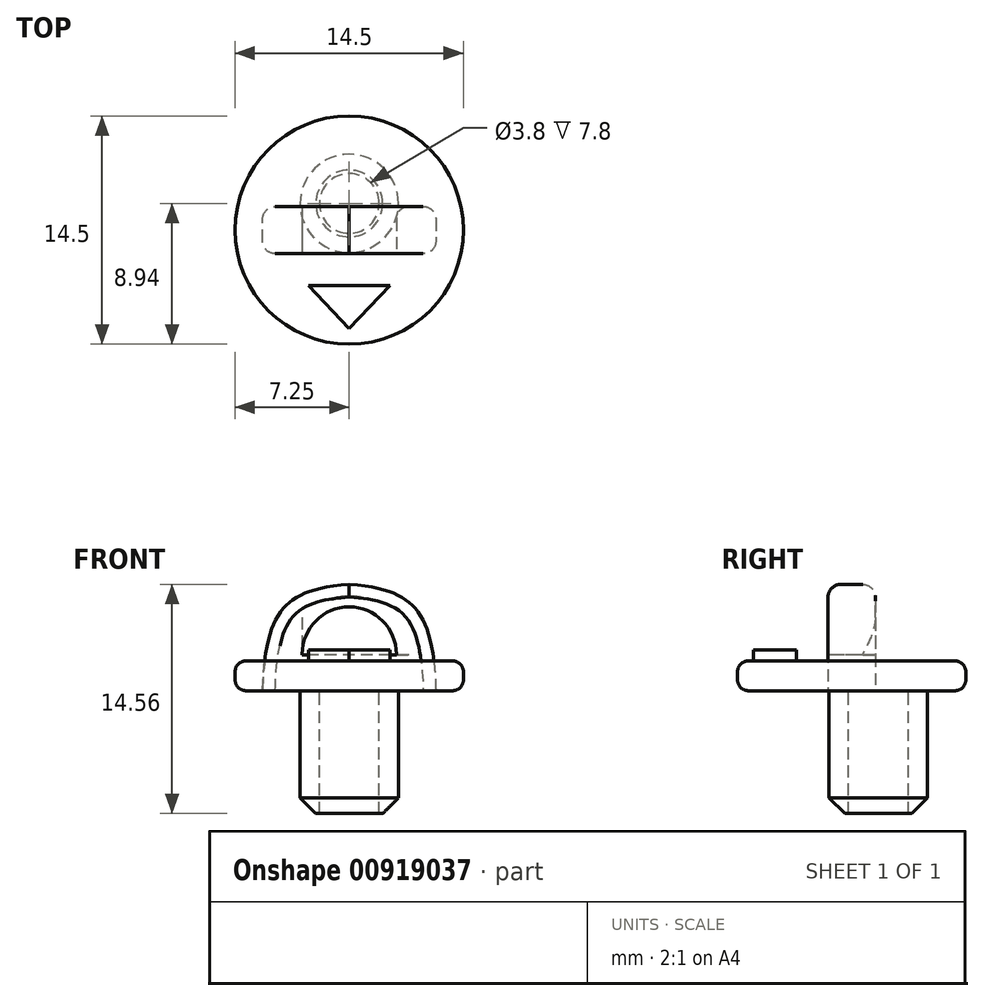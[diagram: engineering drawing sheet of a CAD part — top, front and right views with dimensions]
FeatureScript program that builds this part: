
annotation { "Feature Type Name" : "Feature", "Feature Type Description" : "" }
export const myFeature = defineFeature(function(context is Context, id is Id, definition is map)
    precondition{}
    {
        {
            var Q0;
            Q0=qCreatedBy(makeId("Top.planeOp"),FACE);
            var sketch = newSketch(context, id + "F0", { "sketchPlane" : qUnion([Q0])});
            skCircle(sketch, "E0", {"center": v(0, 0) * mm, "radius": 1.9 * mm});
            skCircle(sketch, "E1", {"center": v(0, 0) * mm, "radius": 3.12 * mm});
            skCircle(sketch, "E2", {"center": v(0, -1.7) * mm, "radius": 7.25 * mm});
            skLineSegment(sketch, "E3.bottom", {"start": v(-5.5, -3.2) * mm, "end": v(5.5, -3.2) * mm});
            skLineSegment(sketch, "E3.top", {"start": v(-5.5, -0.2) * mm, "end": v(5.5, -0.2) * mm});
            skLineSegment(sketch, "E3.left", {"start": v(-5.5, -3.2) * mm, "end": v(-5.5, -0.2) * mm});
            skLineSegment(sketch, "E3.right", {"start": v(5.5, -3.2) * mm, "end": v(5.5, -0.2) * mm});
            skLineSegment(sketch, "E4", {"start": v(0, -7.94) * mm, "end": v(-2.58, -5.2) * mm});
            skLineSegment(sketch, "E5", {"start": v(-2.58, -5.2) * mm, "end": v(2.58, -5.2) * mm});
            skLineSegment(sketch, "E6", {"start": v(2.58, -5.2) * mm, "end": v(0, -7.94) * mm});
            skSolve(sketch);
        }
        {
            var Q0;
            {var subQ0=sQuery(id+"F0.wireOp",EDGE,"E3.bottom");var subQ1=sQuery(id+"F0.wireOp",EDGE,"E0");var subQ2=makeQuery(id+"F0.imprint","INTERSECT",VERTEX,{"disambiguationData":[OD(0.0)],"derivedFrom":[subQ1,subQ0]});Q0=makeQuery(id+"F0.imprint","IMPRINT",FACE,{"disambiguationData":[TD([[makeQuery(id+"F0.imprint","IMPRINT",EDGE,{"disambiguationData":[TD([[subQ2,-1.0]])],"derivedFrom":subQ1}),-1.0]])]});}
            var Q1;
            {var subQ0=sQuery(id+"F0.wireOp",EDGE,"E3.top");var subQ1=sQuery(id+"F0.wireOp",EDGE,"E0");var subQ2=makeQuery(id+"F0.imprint","INTERSECT",VERTEX,{"disambiguationData":[OD(1.0)],"derivedFrom":[subQ1,subQ0]});Q1=makeQuery(id+"F0.imprint","IMPRINT",FACE,{"disambiguationData":[TD([[makeQuery(id+"F0.imprint","IMPRINT",EDGE,{"disambiguationData":[TD([[subQ2,1.0]])],"derivedFrom":subQ1}),-1.0]])]});}
            var Q2;
            {var subQ0=sQuery(id+"F0.wireOp",EDGE,"E3.top");var subQ1=sQuery(id+"F0.wireOp",EDGE,"E0");var subQ2=makeQuery(id+"F0.imprint","INTERSECT",VERTEX,{"disambiguationData":[OD(0.0)],"derivedFrom":[subQ1,subQ0]});Q2=makeQuery(id+"F0.imprint","IMPRINT",FACE,{"disambiguationData":[TD([[makeQuery(id+"F0.imprint","IMPRINT",EDGE,{"disambiguationData":[TD([[subQ2,1.0]])],"derivedFrom":subQ1}),-1.0]])]});}
            var Q3;
            {var subQ0=sQuery(id+"F0.wireOp",EDGE,"E3.top");var subQ1=sQuery(id+"F0.wireOp",EDGE,"E0");var subQ2=makeQuery(id+"F0.imprint","INTERSECT",VERTEX,{"disambiguationData":[OD(0.0)],"derivedFrom":[subQ1,subQ0]});Q3=makeQuery(id+"F0.imprint","IMPRINT",FACE,{"disambiguationData":[TD([[makeQuery(id+"F0.imprint","IMPRINT",EDGE,{"disambiguationData":[TD([[subQ2,-1.0]])],"derivedFrom":subQ1}),-1.0]])]});}
            extrude(context, id + "F1", {"entities" : qUnion([Q0, Q1, Q2, Q3]), "oppositeDirection" : true, "depth" : 7.8 * mm, "offsetDistance" : 25 * mm});
        }
        {
            var Q0;
            {var subQ0=sQuery(id+"F0.wireOp",EDGE,"E3.top");var subQ1=sQuery(id+"F0.wireOp",EDGE,"E0");var subQ2=makeQuery(id+"F0.imprint","INTERSECT",VERTEX,{"disambiguationData":[OD(0.0)],"derivedFrom":[subQ1,subQ0]});Q0=makeQuery(id+"F0.imprint","IMPRINT",FACE,{"disambiguationData":[TD([[makeQuery(id+"F0.imprint","IMPRINT",EDGE,{"disambiguationData":[TD([[subQ2,1.0]])],"derivedFrom":subQ1}),-1.0]])]});}
            var Q1;
            Q1=makeQuery(id+"F0.imprint","IMPRINT",FACE,{"disambiguationData":[TD([[makeQuery(id+"F0.imprint","IMPRINT",EDGE,{"derivedFrom":sQuery(id+"F0.wireOp",EDGE,"E2")}),1.0]])]});
            var Q2;
            {var subQ5=sQuery(id+"F0.wireOp",EDGE,"E3.left");Q2=makeQuery(id+"F0.imprint","IMPRINT",FACE,{"disambiguationData":[TD([[makeQuery(id+"F0.imprint","IMPRINT",EDGE,{"derivedFrom":subQ5}),-1.0]])]});}
            var Q3;
            {var subQ5=sQuery(id+"F0.wireOp",EDGE,"E3.right");Q3=makeQuery(id+"F0.imprint","IMPRINT",FACE,{"disambiguationData":[TD([[makeQuery(id+"F0.imprint","IMPRINT",EDGE,{"derivedFrom":subQ5}),1.0]])]});}
            var Q4;
            {var subQ0=sQuery(id+"F0.wireOp",EDGE,"E3.bottom");var subQ1=sQuery(id+"F0.wireOp",EDGE,"E0");var subQ2=makeQuery(id+"F0.imprint","INTERSECT",VERTEX,{"disambiguationData":[OD(0.0)],"derivedFrom":[subQ1,subQ0]});Q4=makeQuery(id+"F0.imprint","IMPRINT",FACE,{"disambiguationData":[TD([[makeQuery(id+"F0.imprint","IMPRINT",EDGE,{"disambiguationData":[TD([[subQ2,-1.0]])],"derivedFrom":subQ1}),-1.0]])]});}
            var Q5;
            {var subQ0=sQuery(id+"F0.wireOp",EDGE,"E3.top");var subQ1=sQuery(id+"F0.wireOp",EDGE,"E0");var subQ2=makeQuery(id+"F0.imprint","INTERSECT",VERTEX,{"disambiguationData":[OD(1.0)],"derivedFrom":[subQ1,subQ0]});Q5=makeQuery(id+"F0.imprint","IMPRINT",FACE,{"disambiguationData":[TD([[makeQuery(id+"F0.imprint","IMPRINT",EDGE,{"disambiguationData":[TD([[subQ2,1.0]])],"derivedFrom":subQ1}),-1.0]])]});}
            var Q6;
            {var subQ0=sQuery(id+"F0.wireOp",EDGE,"E3.top");var subQ1=sQuery(id+"F0.wireOp",EDGE,"E0");var subQ2=makeQuery(id+"F0.imprint","INTERSECT",VERTEX,{"disambiguationData":[OD(0.0)],"derivedFrom":[subQ1,subQ0]});Q6=makeQuery(id+"F0.imprint","IMPRINT",FACE,{"disambiguationData":[TD([[makeQuery(id+"F0.imprint","IMPRINT",EDGE,{"disambiguationData":[TD([[subQ2,-1.0]])],"derivedFrom":subQ1}),-1.0]])]});}
            var Q7;
            {var subQ0=sQuery(id+"F0.wireOp",EDGE,"E3.top");var subQ1=sQuery(id+"F0.wireOp",EDGE,"E0");var subQ2=makeQuery(id+"F0.imprint","INTERSECT",VERTEX,{"disambiguationData":[OD(0.0)],"derivedFrom":[subQ1,subQ0]});Q7=makeQuery(id+"F0.imprint","IMPRINT",FACE,{"disambiguationData":[TD([[makeQuery(id+"F0.imprint","IMPRINT",EDGE,{"disambiguationData":[TD([[subQ2,-1.0]])],"derivedFrom":subQ1}),1.0]])]});}
            var Q8;
            {var subQ0=sQuery(id+"F0.wireOp",EDGE,"E3.bottom");var subQ1=sQuery(id+"F0.wireOp",EDGE,"E0");var subQ2=makeQuery(id+"F0.imprint","INTERSECT",VERTEX,{"disambiguationData":[OD(0.0)],"derivedFrom":[subQ1,subQ0]});Q8=makeQuery(id+"F0.imprint","IMPRINT",FACE,{"disambiguationData":[TD([[makeQuery(id+"F0.imprint","IMPRINT",EDGE,{"disambiguationData":[TD([[subQ2,-1.0]])],"derivedFrom":subQ1}),1.0]])]});}
            var Q9;
            {var subQ0=sQuery(id+"F0.wireOp",EDGE,"E3.top");var subQ1=sQuery(id+"F0.wireOp",EDGE,"E0");var subQ2=makeQuery(id+"F0.imprint","INTERSECT",VERTEX,{"disambiguationData":[OD(0.0)],"derivedFrom":[subQ1,subQ0]});Q9=makeQuery(id+"F0.imprint","IMPRINT",FACE,{"disambiguationData":[TD([[makeQuery(id+"F0.imprint","IMPRINT",EDGE,{"disambiguationData":[TD([[subQ2,1.0]])],"derivedFrom":subQ1}),1.0]])]});}
            var Q10;
            Q10=makeQuery(id+"F0.imprint","IMPRINT",FACE,{"disambiguationData":[TD([[makeQuery(id+"F0.imprint","IMPRINT",EDGE,{"derivedFrom":sQuery(id+"F0.wireOp",EDGE,"E4")}),-1.0]])]});
            extrude(context, id + "F2", {"entities" : qUnion([Q0, Q1, Q2, Q3, Q4, Q5, Q6, Q7, Q8, Q9, Q10]), "depth" : 1.9 * mm, "offsetDistance" : 25 * mm});
        }
        {
            var Q0;
            {var subQ5=sQuery(id+"F0.wireOp",EDGE,"E3.right");Q0=makeQuery(id+"F0.imprint","IMPRINT",FACE,{"disambiguationData":[TD([[makeQuery(id+"F0.imprint","IMPRINT",EDGE,{"derivedFrom":subQ5}),1.0]])]});}
            var Q1;
            {var subQ5=sQuery(id+"F0.wireOp",EDGE,"E3.left");Q1=makeQuery(id+"F0.imprint","IMPRINT",FACE,{"disambiguationData":[TD([[makeQuery(id+"F0.imprint","IMPRINT",EDGE,{"derivedFrom":subQ5}),-1.0]])]});}
            var Q2;
            {var subQ0=sQuery(id+"F0.wireOp",EDGE,"E3.top");var subQ1=sQuery(id+"F0.wireOp",EDGE,"E0");var subQ2=makeQuery(id+"F0.imprint","INTERSECT",VERTEX,{"disambiguationData":[OD(0.0)],"derivedFrom":[subQ1,subQ0]});Q2=makeQuery(id+"F0.imprint","IMPRINT",FACE,{"disambiguationData":[TD([[makeQuery(id+"F0.imprint","IMPRINT",EDGE,{"disambiguationData":[TD([[subQ2,-1.0]])],"derivedFrom":subQ1}),-1.0]])]});}
            var Q3;
            {var subQ0=sQuery(id+"F0.wireOp",EDGE,"E3.top");var subQ1=sQuery(id+"F0.wireOp",EDGE,"E0");var subQ2=makeQuery(id+"F0.imprint","INTERSECT",VERTEX,{"disambiguationData":[OD(0.0)],"derivedFrom":[subQ1,subQ0]});Q3=makeQuery(id+"F0.imprint","IMPRINT",FACE,{"disambiguationData":[TD([[makeQuery(id+"F0.imprint","IMPRINT",EDGE,{"disambiguationData":[TD([[subQ2,-1.0]])],"derivedFrom":subQ1}),1.0]])]});}
            var Q4;
            {var subQ0=sQuery(id+"F0.wireOp",EDGE,"E3.top");var subQ1=sQuery(id+"F0.wireOp",EDGE,"E0");var subQ2=makeQuery(id+"F0.imprint","INTERSECT",VERTEX,{"disambiguationData":[OD(1.0)],"derivedFrom":[subQ1,subQ0]});Q4=makeQuery(id+"F0.imprint","IMPRINT",FACE,{"disambiguationData":[TD([[makeQuery(id+"F0.imprint","IMPRINT",EDGE,{"disambiguationData":[TD([[subQ2,1.0]])],"derivedFrom":subQ1}),-1.0]])]});}
            extrude(context, id + "F3", {"entities" : qUnion([Q0, Q1, Q2, Q3, Q4]), "depth" : 6.8 * mm, "offsetDistance" : 25 * mm});
        }
        {
            var Q0;
            Q0=makeQuery(id+"F3.opExtrude","CAP_EDGE",EDGE,{"disambiguationData":[OSD([sQuery(id+"F0.wireOp",EDGE,"E3.left")])],"isStart":false});
            var Q1;
            Q1=makeQuery(id+"F3.opExtrude","CAP_EDGE",EDGE,{"disambiguationData":[OSD([sQuery(id+"F0.wireOp",EDGE,"E3.right")])],"isStart":false});
            fillet(context, id + "F4", {"entities" : qUnion([Q0, Q1]), "radius" : 7 * mm, "tangentPropagation" : true, "rho" : .6, "crossSection" : FilletCrossSection.CONIC, "allowEdgeOverflow" : false});
        }
        {
            var Q0;
            Q0=makeQuery(id+"F3.opExtrude","SWEPT_FACE",FACE,{"disambiguationData":[OSD([sQuery(id+"F0.wireOp",EDGE,"E3.bottom")])]});
            var sketch = newSketch(context, id + "F5", { "sketchPlane" : qUnion([Q0])});
            skLineSegment(sketch, "E7.bottom", {"start": v(-3, 2.29) * mm, "end": v(3, 2.29) * mm});
            skLineSegment(sketch, "E7.top", {"start": v(0, 5.33) * mm, "end": v(0, 5.33) * mm});
            skLineSegment(sketch, "E7.left", {"start": v(-3, 2.29) * mm, "end": v(-3, 2.33) * mm});
            skLineSegment(sketch, "E7.right", {"start": v(3, 2.29) * mm, "end": v(3, 2.33) * mm});
            skPoint(sketch, "E7.middle", {"position": v(0, 3.8) * mm});
            skPoint(sketch, "E8.visualSharp", {"position": v(-3, 5.33) * mm});
            skArc(sketch, "E8.filletArc", {"start": v(0, 5.33) * mm, "mid": v(-2.11, 4.45) * mm, "end": v(-3, 2.33) * mm});
            skPoint(sketch, "E9.visualSharp", {"position": v(3, 5.33) * mm});
            skArc(sketch, "E9.filletArc", {"start": v(3, 2.33) * mm, "mid": v(2.11, 4.45) * mm, "end": v(0, 5.33) * mm});
            skSolve(sketch);
        }
        {
            var Q0;
            Q0=makeQuery(id+"F5.imprint","IMPRINT",FACE,{"disambiguationData":[TD([[makeQuery(id+"F5.imprint","IMPRINT",EDGE,{"derivedFrom":sQuery(id+"F5.wireOp",EDGE,"E7.bottom")}),1.0]])]});
            extrude(context, id + "F6", {"entities" : qUnion([Q0]), "operationType" : NewBodyOperationType.REMOVE, "oppositeDirection" : true, "depth" : 25 * mm, "offsetDistance" : 25 * mm});
        }
        {
            var Q0;
            Q0=makeQuery(id+"F6.boolean.opBoolean","COPY",EDGE,{"derivedFrom":makeQuery(id+"F6.opExtrude","CAP_EDGE",EDGE,{"disambiguationData":[OSD([sQuery(id+"F5.wireOp",EDGE,"E7.bottom")])],"isStart":true})});
            var Q1;
            Q1=makeQuery(id+"F6.boolean.opBoolean","COPY",EDGE,{"derivedFrom":makeQuery(id+"F6.opExtrude","CAP_EDGE",EDGE,{"disambiguationData":[OSD([sQuery(id+"F5.wireOp",EDGE,"E7.top")])],"isStart":true})});
            var Q2;
            Q2=makeQuery(id+"F6.boolean.opBoolean","COPY",EDGE,{"derivedFrom":makeQuery(id+"F6.opExtrude","CAP_EDGE",EDGE,{"disambiguationData":[OSD([sQuery(id+"F5.wireOp",EDGE,"E8.filletArc")])],"isStart":true})});
            var Q3;
            Q3=makeQuery(id+"F6.boolean.opBoolean","INTERSECT",EDGE,{"derivedFrom":[makeQuery(id+"F3.opExtrude","SWEPT_FACE",FACE,{"disambiguationData":[OSD([sQuery(id+"F0.wireOp",EDGE,"E3.top")])]}),makeQuery(id+"F6.opExtrude","SWEPT_FACE",FACE,{"disambiguationData":[OSD([sQuery(id+"F5.wireOp",EDGE,"E9.filletArc")])]})]});
            var Q4;
            Q4=makeQuery(id+"F4.opFillet","BLEND_EDGE",EDGE,{"blendedFrom":[makeQuery(id+"F3.opExtrude","CAP_EDGE",EDGE,{"disambiguationData":[OSD([sQuery(id+"F0.wireOp",EDGE,"E3.right")])],"isStart":false}),makeQuery(id+"F3.opExtrude","SWEPT_FACE",FACE,{"disambiguationData":[OSD([sQuery(id+"F0.wireOp",EDGE,"E3.top")])]})],"blendedInto":[makeQuery(id+"F3.opExtrude","SWEPT_FACE",FACE,{"disambiguationData":[OSD([sQuery(id+"F0.wireOp",EDGE,"E3.top")])]})]});
            var Q5;
            Q5=makeQuery(id+"F4.opFillet","BLEND_EDGE",EDGE,{"blendedFrom":[makeQuery(id+"F3.opExtrude","CAP_EDGE",EDGE,{"disambiguationData":[OSD([sQuery(id+"F0.wireOp",EDGE,"E3.left")])],"isStart":false}),makeQuery(id+"F3.opExtrude","SWEPT_FACE",FACE,{"disambiguationData":[OSD([sQuery(id+"F0.wireOp",EDGE,"E3.top")])]})],"blendedInto":[makeQuery(id+"F3.opExtrude","SWEPT_FACE",FACE,{"disambiguationData":[OSD([sQuery(id+"F0.wireOp",EDGE,"E3.top")])]})]});
            var Q6;
            Q6=makeQuery(id+"F4.opFillet","BLEND_EDGE",EDGE,{"blendedFrom":[makeQuery(id+"F3.opExtrude","CAP_EDGE",EDGE,{"disambiguationData":[OSD([sQuery(id+"F0.wireOp",EDGE,"E3.right")])],"isStart":false}),makeQuery(id+"F3.opExtrude","SWEPT_FACE",FACE,{"disambiguationData":[OSD([sQuery(id+"F0.wireOp",EDGE,"E3.bottom")])]})],"blendedInto":[makeQuery(id+"F3.opExtrude","SWEPT_FACE",FACE,{"disambiguationData":[OSD([sQuery(id+"F0.wireOp",EDGE,"E3.bottom")])]})]});
            var Q7;
            Q7=makeQuery(id+"F4.opFillet","BLEND_EDGE",EDGE,{"blendedFrom":[makeQuery(id+"F3.opExtrude","CAP_EDGE",EDGE,{"disambiguationData":[OSD([sQuery(id+"F0.wireOp",EDGE,"E3.left")])],"isStart":false}),makeQuery(id+"F3.opExtrude","SWEPT_FACE",FACE,{"disambiguationData":[OSD([sQuery(id+"F0.wireOp",EDGE,"E3.bottom")])]})],"blendedInto":[makeQuery(id+"F3.opExtrude","SWEPT_FACE",FACE,{"disambiguationData":[OSD([sQuery(id+"F0.wireOp",EDGE,"E3.bottom")])]})]});
            fillet(context, id + "F7", {"entities" : qUnion([Q0, Q1, Q2, Q3, Q4, Q5, Q6, Q7]), "radius" : .8 * mm, "tangentPropagation" : true, "allowEdgeOverflow" : false});
        }
        {
            var Q0;
            Q0=makeQuery(id+"F1.opExtrude","CAP_EDGE",EDGE,{"disambiguationData":[OSD([sQuery(id+"F0.wireOp",EDGE,"E1")])],"isStart":false});
            chamfer(context, id + "F8", {"entities" : qUnion([Q0]), "width" : 1 * mm});
        }
        {
            var Q0;
            Q0=makeQuery(id+"F2.opExtrude","CAP_EDGE",EDGE,{"disambiguationData":[OSD([sQuery(id+"F0.wireOp",EDGE,"E2")])],"isStart":true});
            var Q1;
            Q1=makeQuery(id+"F2.opExtrude","CAP_EDGE",EDGE,{"disambiguationData":[OSD([sQuery(id+"F0.wireOp",EDGE,"E2")])],"isStart":false});
            fillet(context, id + "F9", {"entities" : qUnion([Q0, Q1]), "radius" : .7 * mm, "tangentPropagation" : true, "allowEdgeOverflow" : false});
        }
        {
            var Q0;
            Q0=makeQuery(id+"F0.imprint","IMPRINT",FACE,{"disambiguationData":[TD([[makeQuery(id+"F0.imprint","IMPRINT",EDGE,{"derivedFrom":sQuery(id+"F0.wireOp",EDGE,"E4")}),-1.0]])]});
            extrude(context, id + "F10", {"entities" : qUnion([Q0]), "operationType" : NewBodyOperationType.ADD, "depth" : 2.6 * mm, "offsetDistance" : 25 * mm});
        }
    });
